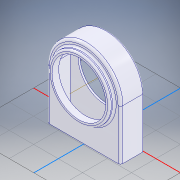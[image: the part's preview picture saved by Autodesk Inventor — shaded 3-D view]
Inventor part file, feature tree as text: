
AUTODESK INVENTOR PART (.ipt)
format: ipt  version: 2022 (Build 260153000, 153)  size: 217,088 bytes
history: native  units: mm
features: sketch x6, extrude x5, other x3, fillet x3, projected_geometry x2, revolve x1
ambient origin geometry x8: Origin, YZ Plane, XZ Plane, XY Plane, X Axis, Y Axis, Z Axis, Center Point
bodies: Body1 (feature_tree)
feature tree (20):
  other  "Твердое тело1"
  extrude  "Выдавливание1"  Depth=60.0mm
  extrude  "Выдавливание2"  Depth=71.0mm
  extrude  "Выдавливание3"  Depth=19.0mm TaperAngle=0.0deg
  fillet  "Сопряжение1"  Radius=44.0mm
  extrude  "Выдавливание4"  Depth=60.0mm
  sketch  "Эскиз5"
  other  "РабПлоскость1"
  extrude  "Выдавливание5"  Depth=8.0mm
  revolve  "Вращение1"
  fillet  "Сопряжение2"  [1 undecoded]
  fillet  "Сопряжение3"  Radius=50.0mm
  sketch  "Эскиз1"
  sketch  "Эскиз2"
  sketch  "Эскиз3"
  sketch  "Эскиз4"
  projected_geometry  "Спроецированная петля1"
  other  "РабОсь1"
  sketch  "Эскиз6"
  projected_geometry  "Спроецированная петля2"
note: 1 required parameter value undecoded (feature->parameter linkage not recoverable at this tier; creation-order binding heuristic only, values carry confidence <= 0.55)
